FCSTD DOCUMENT  (FreeCAD 1.1R14555 (Git shallow))
Label: Instrument_Centipede
License: All rights reserved
LicenseURL: https://en.wikipedia.org/wiki/All_rights_reserved
objects: App::Link×95, App::Point×26, Assembly::AssemblyLink×25, App::FeaturePython×5, Assembly::JointGroup×1, Assembly::AssemblyObject×1
EXTERNAL_REF file=generated_example_K93-10436_all7_withTarantinorinos.FCStd obj=Assembly
EXTERNAL_REF file=generated_example_K93-10436_all7_withTarantinorinos.FCStd obj=K93_120
EXTERNAL_REF file=generated_example_K93-10436_all7_withTarantinorinos.FCStd obj=Reference_all7_1
EXTERNAL_REF file=generated_example_K93-10436_all7_withTarantinorinos.FCStd obj=Body
EXTERNAL_REF file=generated_example_K93-10436_all7_withTarantinorinos.FCStd obj=Assembly001
EXTERNAL_REF file=K93-10436-H7-L120_Tarantinorino_left_withFeet.FCStd obj=_3M_SJ5382
EXTERNAL_REF file=K93-10436-H7-L120_Tarantinorino_left_withFeet.FCStd obj=_3M_SJ5383
EXTERNAL_REF file=K93-10436-H7-L120_Tarantinorino_left_withFeet.FCStd obj=Body
EXTERNAL_REF file=generated_example_K93-10436_all7_withTarantinorinos.FCStd obj=Assembly002
EXTERNAL_REF file=generated_example_K93-10436_all7_withTarantinorinos.FCStd obj=Assembly003
EXTERNAL_REF file=K93-10436-H7-L120_Tarantinorino_right_withFeet.FCStd obj=Body__Mirror__1_
EXTERNAL_REF file=K93-10436-H7-L120_Tarantinorino_right_withFeet.FCStd obj=_3M_SJ5382
EXTERNAL_REF file=K93-10436-H7-L120_Tarantinorino_right_withFeet.FCStd obj=_3M_SJ5383
EXTERNAL_REF file=generated_example_K93-10436_all7_withTarantinorinos.FCStd obj=Assembly004
EXTERNAL_REF file=generated_example_K93-10436_all7_withTarantinorinos.FCStd obj=Body003
EXTERNAL_REF file=generated_example_K93-10436_all7_withTarantinorinos.FCStd obj=Body004
EXTERNAL_REF file=generated_example_K93-10436_all7_withTarantinorinos.FCStd obj=Body005
EXTERNAL_REF file=generated_example_K93-10436_all7_withTarantinorinos.FCStd obj=Body006

FEATURE [App::Point] Origin001
  Role = Origin
FEATURE [App::Point] Origin003
  Role = Origin
FEATURE [App::Link] K93_120  label="K93-120"
  LinkPlacement = pos=(0,126.938,111.562) rot=(1,0,0;1.5708rad)
  LinkedObject = -> <external generated_example_K93-10436_all7_withTarantinorinos.FCStd>#K93_120
  Placement = pos=(0,126.938,111.562) rot=(1,0,0;1.5708rad)
FEATURE [App::Link] Reference_all7_1  label="Reference_all7 1"
  LinkPlacement = pos=(2.87919,6.93809,110.59) rot=(0.99808,0,0;0rad)
  LinkedObject = -> <external generated_example_K93-10436_all7_withTarantinorinos.FCStd>#Reference_all7_1
  Placement = pos=(2.87919,6.93809,110.59) rot=(0.99808,0,0;0rad)
FEATURE [App::Link] Body
  LinkPlacement = pos=(2.87919,-53.8119,119.256) rot=(1,0,0;1.5708rad)
  LinkedObject = -> <external generated_example_K93-10436_all7_withTarantinorinos.FCStd>#Body
  Placement = pos=(2.87919,-53.8119,119.256) rot=(1,0,0;1.5708rad)
FEATURE [App::Point] Origin005  label="Origin006"
  Role = Origin
FEATURE [App::Link] _3M_SJ5382  label="3M_SJ5382"
  LinkPlacement = pos=(-30.6801,-1.9,-31) rot=(0.707107,0.707107,0;3.14159rad)
  LinkedObject = -> <external K93-10436-H7-L120_Tarantinorino_left_withFeet.FCStd>#_3M_SJ5382
  Placement = pos=(-30.6801,-1.9,-31) rot=(0.707107,0.707107,0;3.14159rad)
FEATURE [App::Link] _3M_SJ5383  label="3M_SJ5383"
  LinkPlacement = pos=(-9.29583,-1.9,-4.09999) rot=(0.57735,0.57735,0.57735;2.0944rad)
  LinkedObject = -> <external K93-10436-H7-L120_Tarantinorino_left_withFeet.FCStd>#_3M_SJ5383
  Placement = pos=(-9.29583,-1.9,-4.09999) rot=(0.57735,0.57735,0.57735;2.0944rad)
FEATURE [App::Link] Body001
  LinkPlacement = pos=(-62,-13.9,-4.09999) rot=(1,0,0;1.5708rad)
  LinkedObject = -> <external K93-10436-H7-L120_Tarantinorino_left_withFeet.FCStd>#Body
  Placement = pos=(-62,-13.9,-4.09999) rot=(1,0,0;1.5708rad)
FEATURE [Assembly::AssemblyLink] Assembly002  label="Assembly"
  Group = -> [_3M_SJ5382,_3M_SJ5383,Body001]
  LinkedObject = -> <external generated_example_K93-10436_all7_withTarantinorinos.FCStd>#Assembly001
  Origin = -> Origin004
  Placement = pos=(64.9193,-40.6619,123.46) rot=(0,0,1;0rad)
  Rigid = true
FEATURE [App::Point] Origin007  label="Origin009"
  Role = Origin
FEATURE [App::Link] _3M_SJ5384  label="3M_SJ5384"
  LinkPlacement = pos=(-30.6801,-1.9,-31) rot=(0.707107,0.707107,0;3.14159rad)
  LinkedObject = -> <external K93-10436-H7-L120_Tarantinorino_left_withFeet.FCStd>#_3M_SJ5382
  Placement = pos=(-30.6801,-1.9,-31) rot=(0.707107,0.707107,0;3.14159rad)
FEATURE [App::Link] _3M_SJ5385  label="3M_SJ5385"
  LinkPlacement = pos=(-9.29583,-1.9,-4.09999) rot=(0.57735,0.57735,0.57735;2.0944rad)
  LinkedObject = -> <external K93-10436-H7-L120_Tarantinorino_left_withFeet.FCStd>#_3M_SJ5383
  Placement = pos=(-9.29583,-1.9,-4.09999) rot=(0.57735,0.57735,0.57735;2.0944rad)
FEATURE [App::Link] Body002
  LinkPlacement = pos=(-62,-13.9,-4.09999) rot=(1,0,0;1.5708rad)
  LinkedObject = -> <external K93-10436-H7-L120_Tarantinorino_left_withFeet.FCStd>#Body
  Placement = pos=(-62,-13.9,-4.09999) rot=(1,0,0;1.5708rad)
FEATURE [Assembly::AssemblyLink] Assembly003  label="Assembly"
  Group = -> [_3M_SJ5384,_3M_SJ5385,Body002]
  LinkedObject = -> <external generated_example_K93-10436_all7_withTarantinorinos.FCStd>#Assembly002
  Origin = -> Origin006
  Placement = pos=(-59.1609,54.5381,123.46) rot=(0,0,1;3.14159rad)
  Rigid = true
FEATURE [App::Point] Origin009  label="Origin011"
  Role = Origin
FEATURE [App::Link] Body__Mirror__1_  label="Body (Mirror #1)"
  LinkPlacement = pos=(1.43051e-06,-13.9,-10.1) rot=(1,0,0;1.5708rad)
  LinkedObject = -> <external K93-10436-H7-L120_Tarantinorino_right_withFeet.FCStd>#Body__Mirror__1_
  Placement = pos=(1.43051e-06,-13.9,-10.1) rot=(1,0,0;1.5708rad)
FEATURE [App::Link] _3M_SJ5386  label="3M_SJ5386"
  LinkPlacement = pos=(-31.32,-1.89999,-37) rot=(0.707107,0.707107,0;3.14159rad)
  LinkedObject = -> <external K93-10436-H7-L120_Tarantinorino_right_withFeet.FCStd>#_3M_SJ5382
  Placement = pos=(-31.32,-1.89999,-37) rot=(0.707107,0.707107,0;3.14159rad)
FEATURE [App::Link] _3M_SJ5387  label="3M_SJ5387"
  LinkPlacement = pos=(-52.7042,-1.9,-10.1) rot=(-0.57735,-0.57735,0.57735;2.0944rad)
  LinkedObject = -> <external K93-10436-H7-L120_Tarantinorino_right_withFeet.FCStd>#_3M_SJ5383
  Placement = pos=(-52.7042,-1.9,-10.1) rot=(-0.57735,-0.57735,0.57735;2.0944rad)
FEATURE [Assembly::AssemblyLink] Assembly004  label="Assembly"
  Group = -> [Body__Mirror__1_,_3M_SJ5386,_3M_SJ5387]
  LinkedObject = -> <external generated_example_K93-10436_all7_withTarantinorinos.FCStd>#Assembly003
  Origin = -> Origin008
  Placement = pos=(2.91922,54.5381,129.46) rot=(0,0,1;3.14159rad)
  Rigid = true
FEATURE [App::Point] Origin011  label="Origin014"
  Role = Origin
FEATURE [App::Link] Body__Mirror__1_001  label="Body (Mirror #1)001"
  LinkPlacement = pos=(1.43051e-06,-13.9,-10.1) rot=(1,0,0;1.5708rad)
  LinkedObject = -> <external K93-10436-H7-L120_Tarantinorino_right_withFeet.FCStd>#Body__Mirror__1_
  Placement = pos=(1.43051e-06,-13.9,-10.1) rot=(1,0,0;1.5708rad)
FEATURE [App::Link] _3M_SJ5388  label="3M_SJ5388"
  LinkPlacement = pos=(-31.32,-1.89999,-37) rot=(0.707107,0.707107,0;3.14159rad)
  LinkedObject = -> <external K93-10436-H7-L120_Tarantinorino_right_withFeet.FCStd>#_3M_SJ5382
  Placement = pos=(-31.32,-1.89999,-37) rot=(0.707107,0.707107,0;3.14159rad)
FEATURE [App::Link] _3M_SJ5389  label="3M_SJ5389"
  LinkPlacement = pos=(-52.7042,-1.9,-10.1) rot=(-0.57735,-0.57735,0.57735;2.0944rad)
  LinkedObject = -> <external K93-10436-H7-L120_Tarantinorino_right_withFeet.FCStd>#_3M_SJ5383
  Placement = pos=(-52.7042,-1.9,-10.1) rot=(-0.57735,-0.57735,0.57735;2.0944rad)
FEATURE [Assembly::AssemblyLink] Assembly005  label="Assembly"
  Group = -> [Body__Mirror__1_001,_3M_SJ5388,_3M_SJ5389]
  LinkedObject = -> <external generated_example_K93-10436_all7_withTarantinorinos.FCStd>#Assembly004
  Origin = -> Origin010
  Placement = pos=(2.83915,-40.6619,129.251) rot=(0,0,1;0rad)
  Rigid = true
FEATURE [App::Link] Body003
  LinkPlacement = pos=(2.87919,-56.5619,119.047) rot=(1,0,0;1.5708rad)
  LinkedObject = -> <external generated_example_K93-10436_all7_withTarantinorinos.FCStd>#Body003
  Placement = pos=(2.87919,-56.5619,119.047) rot=(1,0,0;1.5708rad)
FEATURE [App::Link] Body004
  LinkPlacement = pos=(2.87919,-56.5619,119.256) rot=(0,0.707107,-0.707107;3.14159rad)
  LinkedObject = -> <external generated_example_K93-10436_all7_withTarantinorinos.FCStd>#Body004
  Placement = pos=(2.87919,-56.5619,119.256) rot=(0,0.707107,-0.707107;3.14159rad)
FEATURE [App::Link] Body005
  LinkPlacement = pos=(2.87919,70.4381,119.256) rot=(-1,0,0;1.5708rad)
  LinkedObject = -> <external generated_example_K93-10436_all7_withTarantinorinos.FCStd>#Body005
  Placement = pos=(2.87919,70.4381,119.256) rot=(-1,0,0;1.5708rad)
FEATURE [App::Link] Body006
  LinkPlacement = pos=(2.87919,70.4381,119.256) rot=(0,0.707107,0.707107;3.14159rad)
  LinkedObject = -> <external generated_example_K93-10436_all7_withTarantinorinos.FCStd>#Body006
  Placement = pos=(2.87919,70.4381,119.256) rot=(0,0.707107,0.707107;3.14159rad)
FEATURE [Assembly::AssemblyLink] Assembly001  label="Assembly"
  Group = -> [K93_120,Reference_all7_1,Body,Assembly002,Assembly003,Assembly004,Assembly005,Body003,Body004,Body005,Body006]
  LinkedObject = -> <external generated_example_K93-10436_all7_withTarantinorinos.FCStd>#Assembly
  Origin = -> Origin002
  Placement = pos=(-3.48643,-3.86422,0.740982) rot=(0,0,1;0rad)
  Rigid = true
FEATURE [App::Point] Origin013  label="Origin017"
  Role = Origin
FEATURE [App::Link] K93_121  label="K93-121"
  LinkPlacement = pos=(0,126.938,111.562) rot=(1,0,0;1.5708rad)
  LinkedObject = -> <external generated_example_K93-10436_all7_withTarantinorinos.FCStd>#K93_120
  Placement = pos=(0,126.938,111.562) rot=(1,0,0;1.5708rad)
FEATURE [App::Link] Reference_all7_001  label="Reference_all7 001"
  LinkPlacement = pos=(2.87919,6.93809,110.59) rot=(0.99808,0,0;0rad)
  LinkedObject = -> <external generated_example_K93-10436_all7_withTarantinorinos.FCStd>#Reference_all7_1
  Placement = pos=(2.87919,6.93809,110.59) rot=(0.99808,0,0;0rad)
FEATURE [App::Link] Body007
  LinkPlacement = pos=(2.87919,-53.8119,119.256) rot=(1,0,0;1.5708rad)
  LinkedObject = -> <external generated_example_K93-10436_all7_withTarantinorinos.FCStd>#Body
  Placement = pos=(2.87919,-53.8119,119.256) rot=(1,0,0;1.5708rad)
FEATURE [App::Point] Origin015  label="Origin020"
  Role = Origin
FEATURE [App::Link] _3M_SJ5390  label="3M_SJ5390"
  LinkPlacement = pos=(-30.6801,-1.9,-31) rot=(0.707107,0.707107,0;3.14159rad)
  LinkedObject = -> <external K93-10436-H7-L120_Tarantinorino_left_withFeet.FCStd>#_3M_SJ5382
  Placement = pos=(-30.6801,-1.9,-31) rot=(0.707107,0.707107,0;3.14159rad)
FEATURE [App::Link] _3M_SJ5391  label="3M_SJ5391"
  LinkPlacement = pos=(-9.29583,-1.9,-4.09999) rot=(0.57735,0.57735,0.57735;2.0944rad)
  LinkedObject = -> <external K93-10436-H7-L120_Tarantinorino_left_withFeet.FCStd>#_3M_SJ5383
  Placement = pos=(-9.29583,-1.9,-4.09999) rot=(0.57735,0.57735,0.57735;2.0944rad)
FEATURE [App::Link] Body008
  LinkPlacement = pos=(-62,-13.9,-4.09999) rot=(1,0,0;1.5708rad)
  LinkedObject = -> <external K93-10436-H7-L120_Tarantinorino_left_withFeet.FCStd>#Body
  Placement = pos=(-62,-13.9,-4.09999) rot=(1,0,0;1.5708rad)
FEATURE [Assembly::AssemblyLink] Assembly007  label="Assembly"
  Group = -> [_3M_SJ5390,_3M_SJ5391,Body008]
  LinkedObject = -> <external generated_example_K93-10436_all7_withTarantinorinos.FCStd>#Assembly001
  Origin = -> Origin014
  Placement = pos=(64.9193,-40.6619,123.46) rot=(0,0,1;0rad)
  Rigid = true
FEATURE [App::Point] Origin017  label="Origin022"
  Role = Origin
FEATURE [App::Link] _3M_SJ5392  label="3M_SJ5392"
  LinkPlacement = pos=(-30.6801,-1.9,-31) rot=(0.707107,0.707107,0;3.14159rad)
  LinkedObject = -> <external K93-10436-H7-L120_Tarantinorino_left_withFeet.FCStd>#_3M_SJ5382
  Placement = pos=(-30.6801,-1.9,-31) rot=(0.707107,0.707107,0;3.14159rad)
FEATURE [App::Link] _3M_SJ5393  label="3M_SJ5393"
  LinkPlacement = pos=(-9.29583,-1.9,-4.09999) rot=(0.57735,0.57735,0.57735;2.0944rad)
  LinkedObject = -> <external K93-10436-H7-L120_Tarantinorino_left_withFeet.FCStd>#_3M_SJ5383
  Placement = pos=(-9.29583,-1.9,-4.09999) rot=(0.57735,0.57735,0.57735;2.0944rad)
FEATURE [App::Link] Body009
  LinkPlacement = pos=(-62,-13.9,-4.09999) rot=(1,0,0;1.5708rad)
  LinkedObject = -> <external K93-10436-H7-L120_Tarantinorino_left_withFeet.FCStd>#Body
  Placement = pos=(-62,-13.9,-4.09999) rot=(1,0,0;1.5708rad)
FEATURE [Assembly::AssemblyLink] Assembly008  label="Assembly"
  Group = -> [_3M_SJ5392,_3M_SJ5393,Body009]
  LinkedObject = -> <external generated_example_K93-10436_all7_withTarantinorinos.FCStd>#Assembly002
  Origin = -> Origin016
  Placement = pos=(-59.1609,54.5381,123.46) rot=(0,0,1;3.14159rad)
  Rigid = true
FEATURE [App::Point] Origin019  label="Origin025"
  Role = Origin
FEATURE [App::Link] Body__Mirror__1_002  label="Body (Mirror #1)002"
  LinkPlacement = pos=(1.43051e-06,-13.9,-10.1) rot=(1,0,0;1.5708rad)
  LinkedObject = -> <external K93-10436-H7-L120_Tarantinorino_right_withFeet.FCStd>#Body__Mirror__1_
  Placement = pos=(1.43051e-06,-13.9,-10.1) rot=(1,0,0;1.5708rad)
FEATURE [App::Link] _3M_SJ5394  label="3M_SJ5394"
  LinkPlacement = pos=(-31.32,-1.89999,-37) rot=(0.707107,0.707107,0;3.14159rad)
  LinkedObject = -> <external K93-10436-H7-L120_Tarantinorino_right_withFeet.FCStd>#_3M_SJ5382
  Placement = pos=(-31.32,-1.89999,-37) rot=(0.707107,0.707107,0;3.14159rad)
FEATURE [App::Link] _3M_SJ5395  label="3M_SJ5395"
  LinkPlacement = pos=(-52.7042,-1.9,-10.1) rot=(-0.57735,-0.57735,0.57735;2.0944rad)
  LinkedObject = -> <external K93-10436-H7-L120_Tarantinorino_right_withFeet.FCStd>#_3M_SJ5383
  Placement = pos=(-52.7042,-1.9,-10.1) rot=(-0.57735,-0.57735,0.57735;2.0944rad)
FEATURE [Assembly::AssemblyLink] Assembly009  label="Assembly"
  Group = -> [Body__Mirror__1_002,_3M_SJ5394,_3M_SJ5395]
  LinkedObject = -> <external generated_example_K93-10436_all7_withTarantinorinos.FCStd>#Assembly003
  Origin = -> Origin018
  Placement = pos=(2.91922,54.5381,129.46) rot=(0,0,1;3.14159rad)
  Rigid = true
FEATURE [App::Point] Origin021  label="Origin028"
  Role = Origin
FEATURE [App::Link] Body__Mirror__1_003  label="Body (Mirror #1)003"
  LinkPlacement = pos=(1.43051e-06,-13.9,-10.1) rot=(1,0,0;1.5708rad)
  LinkedObject = -> <external K93-10436-H7-L120_Tarantinorino_right_withFeet.FCStd>#Body__Mirror__1_
  Placement = pos=(1.43051e-06,-13.9,-10.1) rot=(1,0,0;1.5708rad)
FEATURE [App::Link] _3M_SJ5396  label="3M_SJ5396"
  LinkPlacement = pos=(-31.32,-1.89999,-37) rot=(0.707107,0.707107,0;3.14159rad)
  LinkedObject = -> <external K93-10436-H7-L120_Tarantinorino_right_withFeet.FCStd>#_3M_SJ5382
  Placement = pos=(-31.32,-1.89999,-37) rot=(0.707107,0.707107,0;3.14159rad)
FEATURE [App::Link] _3M_SJ5397  label="3M_SJ5397"
  LinkPlacement = pos=(-52.7042,-1.9,-10.1) rot=(-0.57735,-0.57735,0.57735;2.0944rad)
  LinkedObject = -> <external K93-10436-H7-L120_Tarantinorino_right_withFeet.FCStd>#_3M_SJ5383
  Placement = pos=(-52.7042,-1.9,-10.1) rot=(-0.57735,-0.57735,0.57735;2.0944rad)
FEATURE [Assembly::AssemblyLink] Assembly010  label="Assembly"
  Group = -> [Body__Mirror__1_003,_3M_SJ5396,_3M_SJ5397]
  LinkedObject = -> <external generated_example_K93-10436_all7_withTarantinorinos.FCStd>#Assembly004
  Origin = -> Origin020
  Placement = pos=(2.83915,-40.6619,129.251) rot=(0,0,1;0rad)
  Rigid = true
FEATURE [App::Link] Body010
  LinkPlacement = pos=(2.87919,-56.5619,119.047) rot=(1,0,0;1.5708rad)
  LinkedObject = -> <external generated_example_K93-10436_all7_withTarantinorinos.FCStd>#Body003
  Placement = pos=(2.87919,-56.5619,119.047) rot=(1,0,0;1.5708rad)
FEATURE [App::Link] Body011
  LinkPlacement = pos=(2.87919,-56.5619,119.256) rot=(0,0.707107,-0.707107;3.14159rad)
  LinkedObject = -> <external generated_example_K93-10436_all7_withTarantinorinos.FCStd>#Body004
  Placement = pos=(2.87919,-56.5619,119.256) rot=(0,0.707107,-0.707107;3.14159rad)
FEATURE [App::Link] Body012
  LinkPlacement = pos=(2.87919,70.4381,119.256) rot=(-1,0,0;1.5708rad)
  LinkedObject = -> <external generated_example_K93-10436_all7_withTarantinorinos.FCStd>#Body005
  Placement = pos=(2.87919,70.4381,119.256) rot=(-1,0,0;1.5708rad)
FEATURE [App::Link] Body013
  LinkPlacement = pos=(2.87919,70.4381,119.256) rot=(0,0.707107,0.707107;3.14159rad)
  LinkedObject = -> <external generated_example_K93-10436_all7_withTarantinorinos.FCStd>#Body006
  Placement = pos=(2.87919,70.4381,119.256) rot=(0,0.707107,0.707107;3.14159rad)
FEATURE [Assembly::AssemblyLink] Assembly006  label="Assembly"
  Group = -> [K93_121,Reference_all7_001,Body007,Assembly007,Assembly008,Assembly009,Assembly010,Body010,Body011,Body012,Body013]
  LinkedObject = -> <external generated_example_K93-10436_all7_withTarantinorinos.FCStd>#Assembly
  Origin = -> Origin012
  Placement = pos=(-3.48643,-3.86423,48.941) rot=(0,0,1;0rad)
  Rigid = true
FEATURE [App::Point] Origin023  label="Origin031"
  Role = Origin
FEATURE [App::Link] K93_122  label="K93-122"
  LinkPlacement = pos=(0,126.938,111.562) rot=(1,0,0;1.5708rad)
  LinkedObject = -> <external generated_example_K93-10436_all7_withTarantinorinos.FCStd>#K93_120
  Placement = pos=(0,126.938,111.562) rot=(1,0,0;1.5708rad)
FEATURE [App::Link] Reference_all7_002  label="Reference_all7 002"
  LinkPlacement = pos=(2.87919,6.93809,110.59) rot=(0.99808,0,0;0rad)
  LinkedObject = -> <external generated_example_K93-10436_all7_withTarantinorinos.FCStd>#Reference_all7_1
  Placement = pos=(2.87919,6.93809,110.59) rot=(0.99808,0,0;0rad)
FEATURE [App::Link] Body014
  LinkPlacement = pos=(2.87919,-53.8119,119.256) rot=(1,0,0;1.5708rad)
  LinkedObject = -> <external generated_example_K93-10436_all7_withTarantinorinos.FCStd>#Body
  Placement = pos=(2.87919,-53.8119,119.256) rot=(1,0,0;1.5708rad)
FEATURE [App::Point] Origin025  label="Origin033"
  Role = Origin
FEATURE [App::Link] _3M_SJ5398  label="3M_SJ5398"
  LinkPlacement = pos=(-30.6801,-1.9,-31) rot=(0.707107,0.707107,0;3.14159rad)
  LinkedObject = -> <external K93-10436-H7-L120_Tarantinorino_left_withFeet.FCStd>#_3M_SJ5382
  Placement = pos=(-30.6801,-1.9,-31) rot=(0.707107,0.707107,0;3.14159rad)
FEATURE [App::Link] _3M_SJ5399  label="3M_SJ5399"
  LinkPlacement = pos=(-9.29583,-1.9,-4.09999) rot=(0.57735,0.57735,0.57735;2.0944rad)
  LinkedObject = -> <external K93-10436-H7-L120_Tarantinorino_left_withFeet.FCStd>#_3M_SJ5383
  Placement = pos=(-9.29583,-1.9,-4.09999) rot=(0.57735,0.57735,0.57735;2.0944rad)
FEATURE [App::Link] Body015
  LinkPlacement = pos=(-62,-13.9,-4.09999) rot=(1,0,0;1.5708rad)
  LinkedObject = -> <external K93-10436-H7-L120_Tarantinorino_left_withFeet.FCStd>#Body
  Placement = pos=(-62,-13.9,-4.09999) rot=(1,0,0;1.5708rad)
FEATURE [Assembly::AssemblyLink] Assembly012  label="Assembly"
  Group = -> [_3M_SJ5398,_3M_SJ5399,Body015]
  LinkedObject = -> <external generated_example_K93-10436_all7_withTarantinorinos.FCStd>#Assembly001
  Origin = -> Origin024
  Placement = pos=(64.9193,-40.6619,123.46) rot=(0,0,1;0rad)
  Rigid = true
FEATURE [App::Point] Origin027  label="Origin036"
  Role = Origin
FEATURE [App::Link] _3M_SJ5400  label="3M_SJ5400"
  LinkPlacement = pos=(-30.6801,-1.9,-31) rot=(0.707107,0.707107,0;3.14159rad)
  LinkedObject = -> <external K93-10436-H7-L120_Tarantinorino_left_withFeet.FCStd>#_3M_SJ5382
  Placement = pos=(-30.6801,-1.9,-31) rot=(0.707107,0.707107,0;3.14159rad)
FEATURE [App::Link] _3M_SJ5401  label="3M_SJ5401"
  LinkPlacement = pos=(-9.29583,-1.9,-4.09999) rot=(0.57735,0.57735,0.57735;2.0944rad)
  LinkedObject = -> <external K93-10436-H7-L120_Tarantinorino_left_withFeet.FCStd>#_3M_SJ5383
  Placement = pos=(-9.29583,-1.9,-4.09999) rot=(0.57735,0.57735,0.57735;2.0944rad)
FEATURE [App::Link] Body016
  LinkPlacement = pos=(-62,-13.9,-4.09999) rot=(1,0,0;1.5708rad)
  LinkedObject = -> <external K93-10436-H7-L120_Tarantinorino_left_withFeet.FCStd>#Body
  Placement = pos=(-62,-13.9,-4.09999) rot=(1,0,0;1.5708rad)
FEATURE [Assembly::AssemblyLink] Assembly013  label="Assembly"
  Group = -> [_3M_SJ5400,_3M_SJ5401,Body016]
  LinkedObject = -> <external generated_example_K93-10436_all7_withTarantinorinos.FCStd>#Assembly002
  Origin = -> Origin026
  Placement = pos=(-59.1609,54.5381,123.46) rot=(0,0,1;3.14159rad)
  Rigid = true
FEATURE [App::Point] Origin029  label="Origin039"
  Role = Origin
FEATURE [App::Link] Body__Mirror__1_004  label="Body (Mirror #1)004"
  LinkPlacement = pos=(1.43051e-06,-13.9,-10.1) rot=(1,0,0;1.5708rad)
  LinkedObject = -> <external K93-10436-H7-L120_Tarantinorino_right_withFeet.FCStd>#Body__Mirror__1_
  Placement = pos=(1.43051e-06,-13.9,-10.1) rot=(1,0,0;1.5708rad)
FEATURE [App::Link] _3M_SJ5402  label="3M_SJ5402"
  LinkPlacement = pos=(-31.32,-1.89999,-37) rot=(0.707107,0.707107,0;3.14159rad)
  LinkedObject = -> <external K93-10436-H7-L120_Tarantinorino_right_withFeet.FCStd>#_3M_SJ5382
  Placement = pos=(-31.32,-1.89999,-37) rot=(0.707107,0.707107,0;3.14159rad)
FEATURE [App::Link] _3M_SJ5403  label="3M_SJ5403"
  LinkPlacement = pos=(-52.7042,-1.9,-10.1) rot=(-0.57735,-0.57735,0.57735;2.0944rad)
  LinkedObject = -> <external K93-10436-H7-L120_Tarantinorino_right_withFeet.FCStd>#_3M_SJ5383
  Placement = pos=(-52.7042,-1.9,-10.1) rot=(-0.57735,-0.57735,0.57735;2.0944rad)
FEATURE [Assembly::AssemblyLink] Assembly014  label="Assembly"
  Group = -> [Body__Mirror__1_004,_3M_SJ5402,_3M_SJ5403]
  LinkedObject = -> <external generated_example_K93-10436_all7_withTarantinorinos.FCStd>#Assembly003
  Origin = -> Origin028
  Placement = pos=(2.91922,54.5381,129.46) rot=(0,0,1;3.14159rad)
  Rigid = true
FEATURE [App::Point] Origin031  label="Origin041"
  Role = Origin
FEATURE [App::Link] Body__Mirror__1_005  label="Body (Mirror #1)005"
  LinkPlacement = pos=(1.43051e-06,-13.9,-10.1) rot=(1,0,0;1.5708rad)
  LinkedObject = -> <external K93-10436-H7-L120_Tarantinorino_right_withFeet.FCStd>#Body__Mirror__1_
  Placement = pos=(1.43051e-06,-13.9,-10.1) rot=(1,0,0;1.5708rad)
FEATURE [App::Link] _3M_SJ5404  label="3M_SJ5404"
  LinkPlacement = pos=(-31.32,-1.89999,-37) rot=(0.707107,0.707107,0;3.14159rad)
  LinkedObject = -> <external K93-10436-H7-L120_Tarantinorino_right_withFeet.FCStd>#_3M_SJ5382
  Placement = pos=(-31.32,-1.89999,-37) rot=(0.707107,0.707107,0;3.14159rad)
FEATURE [App::Link] _3M_SJ5405  label="3M_SJ5405"
  LinkPlacement = pos=(-52.7042,-1.9,-10.1) rot=(-0.57735,-0.57735,0.57735;2.0944rad)
  LinkedObject = -> <external K93-10436-H7-L120_Tarantinorino_right_withFeet.FCStd>#_3M_SJ5383
  Placement = pos=(-52.7042,-1.9,-10.1) rot=(-0.57735,-0.57735,0.57735;2.0944rad)
FEATURE [Assembly::AssemblyLink] Assembly015  label="Assembly"
  Group = -> [Body__Mirror__1_005,_3M_SJ5404,_3M_SJ5405]
  LinkedObject = -> <external generated_example_K93-10436_all7_withTarantinorinos.FCStd>#Assembly004
  Origin = -> Origin030
  Placement = pos=(2.83915,-40.6619,129.251) rot=(0,0,1;0rad)
  Rigid = true
FEATURE [App::Link] Body017
  LinkPlacement = pos=(2.87919,-56.5619,119.047) rot=(1,0,0;1.5708rad)
  LinkedObject = -> <external generated_example_K93-10436_all7_withTarantinorinos.FCStd>#Body003
  Placement = pos=(2.87919,-56.5619,119.047) rot=(1,0,0;1.5708rad)
FEATURE [App::Link] Body018
  LinkPlacement = pos=(2.87919,-56.5619,119.256) rot=(0,0.707107,-0.707107;3.14159rad)
  LinkedObject = -> <external generated_example_K93-10436_all7_withTarantinorinos.FCStd>#Body004
  Placement = pos=(2.87919,-56.5619,119.256) rot=(0,0.707107,-0.707107;3.14159rad)
FEATURE [App::Link] Body019
  LinkPlacement = pos=(2.87919,70.4381,119.256) rot=(-1,0,0;1.5708rad)
  LinkedObject = -> <external generated_example_K93-10436_all7_withTarantinorinos.FCStd>#Body005
  Placement = pos=(2.87919,70.4381,119.256) rot=(-1,0,0;1.5708rad)
FEATURE [App::Link] Body020
  LinkPlacement = pos=(2.87919,70.4381,119.256) rot=(0,0.707107,0.707107;3.14159rad)
  LinkedObject = -> <external generated_example_K93-10436_all7_withTarantinorinos.FCStd>#Body006
  Placement = pos=(2.87919,70.4381,119.256) rot=(0,0.707107,0.707107;3.14159rad)
FEATURE [Assembly::AssemblyLink] Assembly011  label="Assembly"
  Group = -> [K93_122,Reference_all7_002,Body014,Assembly012,Assembly013,Assembly014,Assembly015,Body017,Body018,Body019,Body020]
  LinkedObject = -> <external generated_example_K93-10436_all7_withTarantinorinos.FCStd>#Assembly
  Origin = -> Origin022
  Placement = pos=(-3.48643,-3.86424,97.141) rot=(0,0,1;0rad)
  Rigid = true
FEATURE [App::Point] Origin033  label="Origin044"
  Role = Origin
FEATURE [App::Link] K93_123  label="K93-123"
  LinkPlacement = pos=(0,126.938,111.562) rot=(1,0,0;1.5708rad)
  LinkedObject = -> <external generated_example_K93-10436_all7_withTarantinorinos.FCStd>#K93_120
  Placement = pos=(0,126.938,111.562) rot=(1,0,0;1.5708rad)
FEATURE [App::Link] Reference_all7_003  label="Reference_all7 003"
  LinkPlacement = pos=(2.87919,6.93809,110.59) rot=(0.99808,0,0;0rad)
  LinkedObject = -> <external generated_example_K93-10436_all7_withTarantinorinos.FCStd>#Reference_all7_1
  Placement = pos=(2.87919,6.93809,110.59) rot=(0.99808,0,0;0rad)
FEATURE [App::Link] Body021
  LinkPlacement = pos=(2.87919,-53.8119,119.256) rot=(1,0,0;1.5708rad)
  LinkedObject = -> <external generated_example_K93-10436_all7_withTarantinorinos.FCStd>#Body
  Placement = pos=(2.87919,-53.8119,119.256) rot=(1,0,0;1.5708rad)
FEATURE [App::Point] Origin035  label="Origin047"
  Role = Origin
FEATURE [App::Link] _3M_SJ5406  label="3M_SJ5406"
  LinkPlacement = pos=(-30.6801,-1.9,-31) rot=(0.707107,0.707107,0;3.14159rad)
  LinkedObject = -> <external K93-10436-H7-L120_Tarantinorino_left_withFeet.FCStd>#_3M_SJ5382
  Placement = pos=(-30.6801,-1.9,-31) rot=(0.707107,0.707107,0;3.14159rad)
FEATURE [App::Link] _3M_SJ5407  label="3M_SJ5407"
  LinkPlacement = pos=(-9.29583,-1.9,-4.09999) rot=(0.57735,0.57735,0.57735;2.0944rad)
  LinkedObject = -> <external K93-10436-H7-L120_Tarantinorino_left_withFeet.FCStd>#_3M_SJ5383
  Placement = pos=(-9.29583,-1.9,-4.09999) rot=(0.57735,0.57735,0.57735;2.0944rad)
FEATURE [App::Link] Body022
  LinkPlacement = pos=(-62,-13.9,-4.09999) rot=(1,0,0;1.5708rad)
  LinkedObject = -> <external K93-10436-H7-L120_Tarantinorino_left_withFeet.FCStd>#Body
  Placement = pos=(-62,-13.9,-4.09999) rot=(1,0,0;1.5708rad)
FEATURE [Assembly::AssemblyLink] Assembly017  label="Assembly"
  Group = -> [_3M_SJ5406,_3M_SJ5407,Body022]
  LinkedObject = -> <external generated_example_K93-10436_all7_withTarantinorinos.FCStd>#Assembly001
  Origin = -> Origin034
  Placement = pos=(64.9193,-40.6619,123.46) rot=(0,0,1;0rad)
  Rigid = true
FEATURE [App::Point] Origin037  label="Origin050"
  Role = Origin
FEATURE [App::Link] _3M_SJ5408  label="3M_SJ5408"
  LinkPlacement = pos=(-30.6801,-1.9,-31) rot=(0.707107,0.707107,0;3.14159rad)
  LinkedObject = -> <external K93-10436-H7-L120_Tarantinorino_left_withFeet.FCStd>#_3M_SJ5382
  Placement = pos=(-30.6801,-1.9,-31) rot=(0.707107,0.707107,0;3.14159rad)
FEATURE [App::Link] _3M_SJ5409  label="3M_SJ5409"
  LinkPlacement = pos=(-9.29583,-1.9,-4.09999) rot=(0.57735,0.57735,0.57735;2.0944rad)
  LinkedObject = -> <external K93-10436-H7-L120_Tarantinorino_left_withFeet.FCStd>#_3M_SJ5383
  Placement = pos=(-9.29583,-1.9,-4.09999) rot=(0.57735,0.57735,0.57735;2.0944rad)
FEATURE [App::Link] Body023
  LinkPlacement = pos=(-62,-13.9,-4.09999) rot=(1,0,0;1.5708rad)
  LinkedObject = -> <external K93-10436-H7-L120_Tarantinorino_left_withFeet.FCStd>#Body
  Placement = pos=(-62,-13.9,-4.09999) rot=(1,0,0;1.5708rad)
FEATURE [Assembly::AssemblyLink] Assembly018  label="Assembly"
  Group = -> [_3M_SJ5408,_3M_SJ5409,Body023]
  LinkedObject = -> <external generated_example_K93-10436_all7_withTarantinorinos.FCStd>#Assembly002
  Origin = -> Origin036
  Placement = pos=(-59.1609,54.5381,123.46) rot=(0,0,1;3.14159rad)
  Rigid = true
FEATURE [App::Point] Origin039  label="Origin052"
  Role = Origin
FEATURE [App::Link] Body__Mirror__1_006  label="Body (Mirror #1)006"
  LinkPlacement = pos=(1.43051e-06,-13.9,-10.1) rot=(1,0,0;1.5708rad)
  LinkedObject = -> <external K93-10436-H7-L120_Tarantinorino_right_withFeet.FCStd>#Body__Mirror__1_
  Placement = pos=(1.43051e-06,-13.9,-10.1) rot=(1,0,0;1.5708rad)
FEATURE [App::Link] _3M_SJ5410  label="3M_SJ5410"
  LinkPlacement = pos=(-31.32,-1.89999,-37) rot=(0.707107,0.707107,0;3.14159rad)
  LinkedObject = -> <external K93-10436-H7-L120_Tarantinorino_right_withFeet.FCStd>#_3M_SJ5382
  Placement = pos=(-31.32,-1.89999,-37) rot=(0.707107,0.707107,0;3.14159rad)
FEATURE [App::Link] _3M_SJ5411  label="3M_SJ5411"
  LinkPlacement = pos=(-52.7042,-1.9,-10.1) rot=(-0.57735,-0.57735,0.57735;2.0944rad)
  LinkedObject = -> <external K93-10436-H7-L120_Tarantinorino_right_withFeet.FCStd>#_3M_SJ5383
  Placement = pos=(-52.7042,-1.9,-10.1) rot=(-0.57735,-0.57735,0.57735;2.0944rad)
FEATURE [Assembly::AssemblyLink] Assembly019  label="Assembly"
  Group = -> [Body__Mirror__1_006,_3M_SJ5410,_3M_SJ5411]
  LinkedObject = -> <external generated_example_K93-10436_all7_withTarantinorinos.FCStd>#Assembly003
  Origin = -> Origin038
  Placement = pos=(2.91922,54.5381,129.46) rot=(0,0,1;3.14159rad)
  Rigid = true
FEATURE [App::Point] Origin041  label="Origin055"
  Role = Origin
FEATURE [App::Link] Body__Mirror__1_007  label="Body (Mirror #1)007"
  LinkPlacement = pos=(1.43051e-06,-13.9,-10.1) rot=(1,0,0;1.5708rad)
  LinkedObject = -> <external K93-10436-H7-L120_Tarantinorino_right_withFeet.FCStd>#Body__Mirror__1_
  Placement = pos=(1.43051e-06,-13.9,-10.1) rot=(1,0,0;1.5708rad)
FEATURE [App::Link] _3M_SJ5412  label="3M_SJ5412"
  LinkPlacement = pos=(-31.32,-1.89999,-37) rot=(0.707107,0.707107,0;3.14159rad)
  LinkedObject = -> <external K93-10436-H7-L120_Tarantinorino_right_withFeet.FCStd>#_3M_SJ5382
  Placement = pos=(-31.32,-1.89999,-37) rot=(0.707107,0.707107,0;3.14159rad)
FEATURE [App::Link] _3M_SJ5413  label="3M_SJ5413"
  LinkPlacement = pos=(-52.7042,-1.9,-10.1) rot=(-0.57735,-0.57735,0.57735;2.0944rad)
  LinkedObject = -> <external K93-10436-H7-L120_Tarantinorino_right_withFeet.FCStd>#_3M_SJ5383
  Placement = pos=(-52.7042,-1.9,-10.1) rot=(-0.57735,-0.57735,0.57735;2.0944rad)
FEATURE [Assembly::AssemblyLink] Assembly020  label="Assembly"
  Group = -> [Body__Mirror__1_007,_3M_SJ5412,_3M_SJ5413]
  LinkedObject = -> <external generated_example_K93-10436_all7_withTarantinorinos.FCStd>#Assembly004
  Origin = -> Origin040
  Placement = pos=(2.83915,-40.6619,129.251) rot=(0,0,1;0rad)
  Rigid = true
FEATURE [App::Link] Body024
  LinkPlacement = pos=(2.87919,-56.5619,119.047) rot=(1,0,0;1.5708rad)
  LinkedObject = -> <external generated_example_K93-10436_all7_withTarantinorinos.FCStd>#Body003
  Placement = pos=(2.87919,-56.5619,119.047) rot=(1,0,0;1.5708rad)
FEATURE [App::Link] Body025
  LinkPlacement = pos=(2.87919,-56.5619,119.256) rot=(0,0.707107,-0.707107;3.14159rad)
  LinkedObject = -> <external generated_example_K93-10436_all7_withTarantinorinos.FCStd>#Body004
  Placement = pos=(2.87919,-56.5619,119.256) rot=(0,0.707107,-0.707107;3.14159rad)
FEATURE [App::Link] Body026
  LinkPlacement = pos=(2.87919,70.4381,119.256) rot=(-1,0,0;1.5708rad)
  LinkedObject = -> <external generated_example_K93-10436_all7_withTarantinorinos.FCStd>#Body005
  Placement = pos=(2.87919,70.4381,119.256) rot=(-1,0,0;1.5708rad)
FEATURE [App::Link] Body027
  LinkPlacement = pos=(2.87919,70.4381,119.256) rot=(0,0.707107,0.707107;3.14159rad)
  LinkedObject = -> <external generated_example_K93-10436_all7_withTarantinorinos.FCStd>#Body006
  Placement = pos=(2.87919,70.4381,119.256) rot=(0,0.707107,0.707107;3.14159rad)
FEATURE [Assembly::AssemblyLink] Assembly016  label="Assembly"
  Group = -> [K93_123,Reference_all7_003,Body021,Assembly017,Assembly018,Assembly019,Assembly020,Body024,Body025,Body026,Body027]
  LinkedObject = -> <external generated_example_K93-10436_all7_withTarantinorinos.FCStd>#Assembly
  Origin = -> Origin032
  Placement = pos=(-3.48643,-3.86424,145.341) rot=(0,0,1;0rad)
  Rigid = true
FEATURE [App::Point] Origin043  label="Origin058"
  Role = Origin
FEATURE [App::Link] K93_124  label="K93-124"
  LinkPlacement = pos=(0,126.938,111.562) rot=(1,0,0;1.5708rad)
  LinkedObject = -> <external generated_example_K93-10436_all7_withTarantinorinos.FCStd>#K93_120
  Placement = pos=(0,126.938,111.562) rot=(1,0,0;1.5708rad)
FEATURE [App::Link] Reference_all7_004  label="Reference_all7 004"
  LinkPlacement = pos=(2.87919,6.93809,110.59) rot=(0.99808,0,0;0rad)
  LinkedObject = -> <external generated_example_K93-10436_all7_withTarantinorinos.FCStd>#Reference_all7_1
  Placement = pos=(2.87919,6.93809,110.59) rot=(0.99808,0,0;0rad)
FEATURE [App::Link] Body028
  LinkPlacement = pos=(2.87919,-53.8119,119.256) rot=(1,0,0;1.5708rad)
  LinkedObject = -> <external generated_example_K93-10436_all7_withTarantinorinos.FCStd>#Body
  Placement = pos=(2.87919,-53.8119,119.256) rot=(1,0,0;1.5708rad)
FEATURE [App::Point] Origin045  label="Origin061"
  Role = Origin
FEATURE [App::Link] _3M_SJ5414  label="3M_SJ5414"
  LinkPlacement = pos=(-30.6801,-1.9,-31) rot=(0.707107,0.707107,0;3.14159rad)
  LinkedObject = -> <external K93-10436-H7-L120_Tarantinorino_left_withFeet.FCStd>#_3M_SJ5382
  Placement = pos=(-30.6801,-1.9,-31) rot=(0.707107,0.707107,0;3.14159rad)
FEATURE [App::Link] _3M_SJ5415  label="3M_SJ5415"
  LinkPlacement = pos=(-9.29583,-1.9,-4.09999) rot=(0.57735,0.57735,0.57735;2.0944rad)
  LinkedObject = -> <external K93-10436-H7-L120_Tarantinorino_left_withFeet.FCStd>#_3M_SJ5383
  Placement = pos=(-9.29583,-1.9,-4.09999) rot=(0.57735,0.57735,0.57735;2.0944rad)
FEATURE [App::Link] Body029
  LinkPlacement = pos=(-62,-13.9,-4.09999) rot=(1,0,0;1.5708rad)
  LinkedObject = -> <external K93-10436-H7-L120_Tarantinorino_left_withFeet.FCStd>#Body
  Placement = pos=(-62,-13.9,-4.09999) rot=(1,0,0;1.5708rad)
FEATURE [Assembly::AssemblyLink] Assembly022  label="Assembly"
  Group = -> [_3M_SJ5414,_3M_SJ5415,Body029]
  LinkedObject = -> <external generated_example_K93-10436_all7_withTarantinorinos.FCStd>#Assembly001
  Origin = -> Origin044
  Placement = pos=(64.9193,-40.6619,123.46) rot=(0,0,1;0rad)
  Rigid = true
FEATURE [App::Point] Origin047  label="Origin063"
  Role = Origin
FEATURE [App::Link] _3M_SJ5416  label="3M_SJ5416"
  LinkPlacement = pos=(-30.6801,-1.9,-31) rot=(0.707107,0.707107,0;3.14159rad)
  LinkedObject = -> <external K93-10436-H7-L120_Tarantinorino_left_withFeet.FCStd>#_3M_SJ5382
  Placement = pos=(-30.6801,-1.9,-31) rot=(0.707107,0.707107,0;3.14159rad)
FEATURE [App::Link] _3M_SJ5417  label="3M_SJ5417"
  LinkPlacement = pos=(-9.29583,-1.9,-4.09999) rot=(0.57735,0.57735,0.57735;2.0944rad)
  LinkedObject = -> <external K93-10436-H7-L120_Tarantinorino_left_withFeet.FCStd>#_3M_SJ5383
  Placement = pos=(-9.29583,-1.9,-4.09999) rot=(0.57735,0.57735,0.57735;2.0944rad)
FEATURE [App::Link] Body030
  LinkPlacement = pos=(-62,-13.9,-4.09999) rot=(1,0,0;1.5708rad)
  LinkedObject = -> <external K93-10436-H7-L120_Tarantinorino_left_withFeet.FCStd>#Body
  Placement = pos=(-62,-13.9,-4.09999) rot=(1,0,0;1.5708rad)
FEATURE [Assembly::AssemblyLink] Assembly023  label="Assembly"
  Group = -> [_3M_SJ5416,_3M_SJ5417,Body030]
  LinkedObject = -> <external generated_example_K93-10436_all7_withTarantinorinos.FCStd>#Assembly002
  Origin = -> Origin046
  Placement = pos=(-59.1609,54.5381,123.46) rot=(0,0,1;3.14159rad)
  Rigid = true
FEATURE [App::Point] Origin049  label="Origin066"
  Role = Origin
FEATURE [App::Link] Body__Mirror__1_008  label="Body (Mirror #1)008"
  LinkPlacement = pos=(1.43051e-06,-13.9,-10.1) rot=(1,0,0;1.5708rad)
  LinkedObject = -> <external K93-10436-H7-L120_Tarantinorino_right_withFeet.FCStd>#Body__Mirror__1_
  Placement = pos=(1.43051e-06,-13.9,-10.1) rot=(1,0,0;1.5708rad)
FEATURE [App::Link] _3M_SJ5418  label="3M_SJ5418"
  LinkPlacement = pos=(-31.32,-1.89999,-37) rot=(0.707107,0.707107,0;3.14159rad)
  LinkedObject = -> <external K93-10436-H7-L120_Tarantinorino_right_withFeet.FCStd>#_3M_SJ5382
  Placement = pos=(-31.32,-1.89999,-37) rot=(0.707107,0.707107,0;3.14159rad)
FEATURE [App::Link] _3M_SJ5419  label="3M_SJ5419"
  LinkPlacement = pos=(-52.7042,-1.9,-10.1) rot=(-0.57735,-0.57735,0.57735;2.0944rad)
  LinkedObject = -> <external K93-10436-H7-L120_Tarantinorino_right_withFeet.FCStd>#_3M_SJ5383
  Placement = pos=(-52.7042,-1.9,-10.1) rot=(-0.57735,-0.57735,0.57735;2.0944rad)
FEATURE [Assembly::AssemblyLink] Assembly024  label="Assembly"
  Group = -> [Body__Mirror__1_008,_3M_SJ5418,_3M_SJ5419]
  LinkedObject = -> <external generated_example_K93-10436_all7_withTarantinorinos.FCStd>#Assembly003
  Origin = -> Origin048
  Placement = pos=(2.91922,54.5381,129.46) rot=(0,0,1;3.14159rad)
  Rigid = true
FEATURE [App::Point] Origin051  label="Origin069"
  Role = Origin
FEATURE [App::Link] Body__Mirror__1_009  label="Body (Mirror #1)009"
  LinkPlacement = pos=(1.43051e-06,-13.9,-10.1) rot=(1,0,0;1.5708rad)
  LinkedObject = -> <external K93-10436-H7-L120_Tarantinorino_right_withFeet.FCStd>#Body__Mirror__1_
  Placement = pos=(1.43051e-06,-13.9,-10.1) rot=(1,0,0;1.5708rad)
FEATURE [App::Link] _3M_SJ5420  label="3M_SJ5420"
  LinkPlacement = pos=(-31.32,-1.89999,-37) rot=(0.707107,0.707107,0;3.14159rad)
  LinkedObject = -> <external K93-10436-H7-L120_Tarantinorino_right_withFeet.FCStd>#_3M_SJ5382
  Placement = pos=(-31.32,-1.89999,-37) rot=(0.707107,0.707107,0;3.14159rad)
FEATURE [App::Link] _3M_SJ5421  label="3M_SJ5421"
  LinkPlacement = pos=(-52.7042,-1.9,-10.1) rot=(-0.57735,-0.57735,0.57735;2.0944rad)
  LinkedObject = -> <external K93-10436-H7-L120_Tarantinorino_right_withFeet.FCStd>#_3M_SJ5383
  Placement = pos=(-52.7042,-1.9,-10.1) rot=(-0.57735,-0.57735,0.57735;2.0944rad)
FEATURE [Assembly::AssemblyLink] Assembly025  label="Assembly"
  Group = -> [Body__Mirror__1_009,_3M_SJ5420,_3M_SJ5421]
  LinkedObject = -> <external generated_example_K93-10436_all7_withTarantinorinos.FCStd>#Assembly004
  Origin = -> Origin050
  Placement = pos=(2.83915,-40.6619,129.251) rot=(0,0,1;0rad)
  Rigid = true
FEATURE [App::Link] Body031
  LinkPlacement = pos=(2.87919,-56.5619,119.047) rot=(1,0,0;1.5708rad)
  LinkedObject = -> <external generated_example_K93-10436_all7_withTarantinorinos.FCStd>#Body003
  Placement = pos=(2.87919,-56.5619,119.047) rot=(1,0,0;1.5708rad)
FEATURE [App::Link] Body032
  LinkPlacement = pos=(2.87919,-56.5619,119.256) rot=(0,0.707107,-0.707107;3.14159rad)
  LinkedObject = -> <external generated_example_K93-10436_all7_withTarantinorinos.FCStd>#Body004
  Placement = pos=(2.87919,-56.5619,119.256) rot=(0,0.707107,-0.707107;3.14159rad)
FEATURE [App::Link] Body033
  LinkPlacement = pos=(2.87919,70.4381,119.256) rot=(-1,0,0;1.5708rad)
  LinkedObject = -> <external generated_example_K93-10436_all7_withTarantinorinos.FCStd>#Body005
  Placement = pos=(2.87919,70.4381,119.256) rot=(-1,0,0;1.5708rad)
FEATURE [App::Link] Body034
  LinkPlacement = pos=(2.87919,70.4381,119.256) rot=(0,0.707107,0.707107;3.14159rad)
  LinkedObject = -> <external generated_example_K93-10436_all7_withTarantinorinos.FCStd>#Body006
  Placement = pos=(2.87919,70.4381,119.256) rot=(0,0.707107,0.707107;3.14159rad)
FEATURE [Assembly::AssemblyLink] Assembly021  label="Assembly"
  Group = -> [K93_124,Reference_all7_004,Body028,Assembly022,Assembly023,Assembly024,Assembly025,Body031,Body032,Body033,Body034]
  LinkedObject = -> <external generated_example_K93-10436_all7_withTarantinorinos.FCStd>#Assembly
  Origin = -> Origin042
  Placement = pos=(-3.48643,-3.86425,193.541) rot=(0,0,1;0rad)
  Rigid = true
FEATURE [App::FeaturePython] Joint  label="Fixed"  # Assembly joint (typed FeaturePython)
  Angle = 0
  AngleMax = 0
  AngleMin = 0
  Detach1 = false
  Detach2 = false
  Distance = 0
  Distance2 = 0
  EnableAngleMax = false
  EnableAngleMin = false
  EnableLengthMax = false
  EnableLengthMin = false
  JointType = 0 (Fixed)
  LengthMax = 0
  LengthMin = 0
  Placement1 = pos=(31.32,-24.1,1) rot=(0.707107,0,0.707107;3.14159rad)
  Placement2 = pos=(31.32,24.1,1) rot=(0.707107,0,0.707107;3.14159rad)
  Reference1 = -> Assembly [Assembly006.Assembly007.Body008.Edge120,Assembly006.Assembly007.Body008.Edge120]
  Reference2 = -> Assembly [Assembly001.Assembly002.Body001.Edge112,Assembly001.Assembly002.Body001.Edge112]
  Suppressed = false
FEATURE [App::FeaturePython] GroundedJoint  # Assembly grounded joint (typed FeaturePython)
  ObjectToGround = -> Assembly001
FEATURE [App::FeaturePython] Joint001  label="Fixed001"  # Assembly joint (typed FeaturePython)
  Angle = 0
  AngleMax = 0
  AngleMin = 0
  Detach1 = false
  Detach2 = false
  Distance = 0
  Distance2 = 0
  EnableAngleMax = false
  EnableAngleMin = false
  EnableLengthMax = false
  EnableLengthMin = false
  JointType = 0 (Fixed)
  LengthMax = 0
  LengthMin = 0
  Placement1 = pos=(31.32,-24.1,1) rot=(0.707107,0,0.707107;3.14159rad)
  Placement2 = pos=(31.32,24.1,1) rot=(0.707107,0,0.707107;3.14159rad)
  Reference1 = -> Assembly [Assembly011.Assembly012.Body015.Edge120,Assembly011.Assembly012.Body015.Edge120]
  Reference2 = -> Assembly [Assembly006.Assembly007.Body008.Edge112,Assembly006.Assembly007.Body008.Edge112]
  Suppressed = false
FEATURE [App::FeaturePython] Joint002  label="Fixed002"  # Assembly joint (typed FeaturePython)
  Angle = 0
  AngleMax = 0
  AngleMin = 0
  Detach1 = false
  Detach2 = false
  Distance = 0
  Distance2 = 0
  EnableAngleMax = false
  EnableAngleMin = false
  EnableLengthMax = false
  EnableLengthMin = false
  JointType = 0 (Fixed)
  LengthMax = 0
  LengthMin = 0
  Placement1 = pos=(31.32,24.1,1) rot=(0.707107,0,0.707107;3.14159rad)
  Placement2 = pos=(31.32,-24.1,1) rot=(0.707107,0,0.707107;3.14159rad)
  Reference1 = -> Assembly [Assembly011.Assembly012.Body015.Edge112,Assembly011.Assembly012.Body015.Edge112]
  Reference2 = -> Assembly [Assembly016.Assembly017.Body022.Edge120,Assembly016.Assembly017.Body022.Edge120]
  Suppressed = false
FEATURE [App::FeaturePython] Joint003  label="Fixed003"  # Assembly joint (typed FeaturePython)
  Angle = 0
  AngleMax = 0
  AngleMin = 0
  Detach1 = false
  Detach2 = false
  Distance = 0
  Distance2 = 0
  EnableAngleMax = false
  EnableAngleMin = false
  EnableLengthMax = false
  EnableLengthMin = false
  JointType = 0 (Fixed)
  LengthMax = 0
  LengthMin = 0
  Placement1 = pos=(31.32,-24.1,1) rot=(0.707107,0,0.707107;3.14159rad)
  Placement2 = pos=(31.32,24.1,1) rot=(0.707107,0,0.707107;3.14159rad)
  Reference1 = -> Assembly [Assembly021.Assembly022.Body029.Edge120,Assembly021.Assembly022.Body029.Edge120]
  Reference2 = -> Assembly [Assembly016.Assembly017.Body022.Edge112,Assembly016.Assembly017.Body022.Edge112]
  Suppressed = false
FEATURE [Assembly::JointGroup] Joints
  Group = -> [Joint,GroundedJoint,Joint001,Joint002,Joint003]
FEATURE [Assembly::AssemblyObject] Assembly
  Group = -> [Joints,Assembly001,Assembly006,Assembly011,Assembly016,Assembly021,Joint,GroundedJoint,Joint001,Joint002,Joint003]
  Origin = -> Origin
  Type = Assembly

RESOLVED EXTERNAL PARTS (link-assembly join: the EXTERNAL_REF files above that resolve inside this repo's crawl, each included once):
---- part K93-10436-H7-L120_Tarantinorino_left_withFeet.FCStd = doc fcstd_c7ecf6655185 ----
FCSTD DOCUMENT  (FreeCAD 1.1R20251031 (Git shallow))
Label: K93-10436-H7-L120_Tarantinorino_left_withFeet
License: All rights reserved
LicenseURL: https://en.wikipedia.org/wiki/All_rights_reserved
objects: App::Link×3, App::FeaturePython×3, App::Point×1, Assembly::JointGroup×1, Assembly::AssemblyObject×1
EXTERNAL_REF file=K93-10436-H7-L120_Tarantinorino_left.FCStd obj=Body
EXTERNAL_REF file=3M_SJ5382.FCStd obj=Body

FEATURE [App::Point] Origin001
  Role = Origin
FEATURE [App::Link] Body
  LinkPlacement = pos=(-62,-13.9,-4.09999) rot=(1,0,0;1.5708rad)
  LinkedObject = -> <external K93-10436-H7-L120_Tarantinorino_left.FCStd>#Body
  Placement = pos=(-62,-13.9,-4.09999) rot=(1,0,0;1.5708rad)
FEATURE [App::FeaturePython] GroundedJoint  label="GroundedJoint001"  # Assembly grounded joint (typed FeaturePython)
  ObjectToGround = -> Body
FEATURE [App::Link] _3M_SJ5382  label="3M_SJ5382"
  LinkPlacement = pos=(-9.29583,-1.9,-4.09999) rot=(0.57735,0.57735,0.57735;2.0944rad)
  LinkedObject = -> <external 3M_SJ5382.FCStd>#Body
  Placement = pos=(-9.29583,-1.9,-4.09999) rot=(0.57735,0.57735,0.57735;2.0944rad)
FEATURE [App::FeaturePython] Joint  label="Fixed"  # Assembly joint (typed FeaturePython)
  Angle = 0
  AngleMax = 0
  AngleMin = 0
  Detach1 = false
  Detach2 = false
  Distance = 0
  Distance2 = 0
  EnableAngleMax = false
  EnableAngleMin = false
  EnableLengthMax = false
  EnableLengthMin = false
  JointType = 0 (Fixed)
  LengthMax = 0
  LengthMin = 0
  Placement1 = pos=(52.7042,1.8e-15,-12) rot=(-0.707107,0,-0.707107;3.14159rad)
  Placement2 = pos=(0,0,0) rot=(0,0,-1;3.14159rad)
  Reference1 = -> Assembly [Body.Face83,Body.Face83]
  Reference2 = -> Assembly [_3M_SJ5382.Face3,_3M_SJ5382.Face3]
  Suppressed = false
FEATURE [App::Link] _3M_SJ5383  label="3M_SJ5383"
  LinkPlacement = pos=(-30.6801,-1.9,-32.2) rot=(0.707107,-0.707107,0;3.14159rad)
  LinkedObject = -> <external 3M_SJ5382.FCStd>#Body
  Placement = pos=(-30.6801,-1.9,-32.2) rot=(0.707107,-0.707107,0;3.14159rad)
FEATURE [App::FeaturePython] Joint001  label="Fixed004"  # Assembly joint (typed FeaturePython)
  Angle = 0
  AngleMax = 0
  AngleMin = 0
  Detach1 = false
  Detach2 = false
  Distance = 0
  Distance2 = 0
  EnableAngleMax = false
  EnableAngleMin = false
  EnableLengthMax = false
  EnableLengthMin = false
  JointType = 0 (Fixed)
  LengthMax = 0
  LengthMin = 0
  Placement1 = pos=(0,0,0) rot=(-1,0,0;3.14159rad)
  Placement2 = pos=(31.32,-28.1,-12) rot=(-0.57735,-0.57735,-0.57735;2.0944rad)
  Reference1 = -> Assembly [_3M_SJ5383.Edge4,_3M_SJ5383.Edge4]
  Reference2 = -> Assembly [Body.Face129,Body.Face129]
  Suppressed = false
FEATURE [Assembly::JointGroup] Joints
  Group = -> [GroundedJoint,Joint,Joint001]
FEATURE [Assembly::AssemblyObject] Assembly
  Group = -> [Joints,Body,GroundedJoint,_3M_SJ5382,Joint,_3M_SJ5383,Joint001]
  Origin = -> Origin
  Type = Assembly
---- part K93-10436-H7-L120_Tarantinorino_right_withFeet.FCStd = doc fcstd_a3d1782a5d18 ----
FCSTD DOCUMENT  (FreeCAD 1.1R20251031 (Git shallow))
Label: K93-10436-H7-L120_Tarantinorino_right_withFeet
License: All rights reserved
LicenseURL: https://en.wikipedia.org/wiki/All_rights_reserved
objects: App::Link×3, App::FeaturePython×3, App::Point×1, Assembly::JointGroup×1, Assembly::AssemblyObject×1
EXTERNAL_REF file=K93-10436-H7-L120_Tarantinorino_right.FCStd obj=Part__Mirroring
EXTERNAL_REF file=3M_SJ5382.FCStd obj=Body

FEATURE [App::Point] Origin001
  Role = Origin
FEATURE [App::Link] Body__Mirror__1_  label="Body (Mirror #1)"
  LinkPlacement = pos=(1.43051e-06,-13.9,-10.1) rot=(1,0,0;1.5708rad)
  LinkedObject = -> <external K93-10436-H7-L120_Tarantinorino_right.FCStd>#Part__Mirroring
  Placement = pos=(1.43051e-06,-13.9,-10.1) rot=(1,0,0;1.5708rad)
FEATURE [App::FeaturePython] GroundedJoint  # Assembly grounded joint (typed FeaturePython)
  ObjectToGround = -> Body__Mirror__1_
FEATURE [App::Link] _3M_SJ5382  label="3M_SJ5382"
  LinkPlacement = pos=(-31.32,-1.89999,-37) rot=(0.707107,0.707107,0;3.14159rad)
  LinkedObject = -> <external 3M_SJ5382.FCStd>#Body
  Placement = pos=(-31.32,-1.89999,-37) rot=(0.707107,0.707107,0;3.14159rad)
FEATURE [App::FeaturePython] Joint  label="Fixed"  # Assembly joint (typed FeaturePython)
  Angle = 0
  AngleMax = 0
  AngleMin = 0
  Detach1 = false
  Detach2 = false
  Distance = 0
  Distance2 = 0
  EnableAngleMax = false
  EnableAngleMin = false
  EnableLengthMax = false
  EnableLengthMin = false
  JointType = 0 (Fixed)
  LengthMax = 0
  LengthMin = 0
  Placement1 = pos=(-31.32,-26.9,-12) rot=(-0.57735,0.57735,-0.57735;4.18879rad)
  Placement2 = pos=(0,0,0) rot=(0,0,-1;3.14159rad)
  Reference1 = -> Assembly [Body__Mirror__1_.Face111,Body__Mirror__1_.Face111]
  Reference2 = -> Assembly [_3M_SJ5382.?Face3,_3M_SJ5382.?Edge1]
  Suppressed = false
FEATURE [App::Link] _3M_SJ5383  label="3M_SJ5383"
  LinkPlacement = pos=(-52.7042,-1.9,-10.1) rot=(-0.57735,-0.57735,0.57735;2.0944rad)
  LinkedObject = -> <external 3M_SJ5382.FCStd>#Body
  Placement = pos=(-52.7042,-1.9,-10.1) rot=(-0.57735,-0.57735,0.57735;2.0944rad)
FEATURE [App::FeaturePython] Joint001  label="Fixed001"  # Assembly joint (typed FeaturePython)
  Angle = 0
  AngleMax = 0
  AngleMin = 0
  Detach1 = false
  Detach2 = false
  Distance = 0
  Distance2 = 0
  EnableAngleMax = false
  EnableAngleMin = false
  EnableLengthMax = false
  EnableLengthMin = false
  JointType = 0 (Fixed)
  LengthMax = 0
  LengthMin = 0
  Placement1 = pos=(-52.7042,0,-12) rot=(-0.707107,0,-0.707107;3.14159rad)
  Placement2 = pos=(0,0,0) rot=(0,0,1;3.14159rad)
  Reference1 = -> Assembly [Body__Mirror__1_.Face106,Body__Mirror__1_.Face106]
  Reference2 = -> Assembly [_3M_SJ5383.?Face3,_3M_SJ5383.?Face3]
  Suppressed = false
FEATURE [Assembly::JointGroup] Joints
  Group = -> [GroundedJoint,Joint,Joint001]
FEATURE [Assembly::AssemblyObject] Assembly
  Group = -> [Joints,Body__Mirror__1_,GroundedJoint,_3M_SJ5382,Joint,_3M_SJ5383,Joint001]
  Origin = -> Origin
  Type = Assembly
---- part generated_example_K93-10436_all7_withTarantinorinos.FCStd = doc fcstd_a31de3788964 ----
FCSTD DOCUMENT  (FreeCAD 1.1R20251031 (Git shallow))
Label: generated_example_K93-10436_all7_withTarantinorinos
License: All rights reserved
LicenseURL: https://en.wikipedia.org/wiki/All_rights_reserved
objects: App::Link×19, App::FeaturePython×14, App::Point×5, Assembly::AssemblyLink×4, Assembly::JointGroup×1, Assembly::AssemblyObject×1
EXTERNAL_REF file=K93-10436-H7-L120.FCStd obj=K93_120
EXTERNAL_REF file=Reference_all7.FCStd obj=Reference_all7_1
EXTERNAL_REF file=K93-10436-H7-L120_frontpanel_generated_example.FCStd obj=Body
EXTERNAL_REF file=K93-10436-H7-L120_Tarantinorino_left_withFeet.FCStd obj=Assembly
EXTERNAL_REF file=K93-10436-H7-L120_Tarantinorino_left_withFeet.FCStd obj=_3M_SJ5382
EXTERNAL_REF file=K93-10436-H7-L120_Tarantinorino_left_withFeet.FCStd obj=_3M_SJ5383
EXTERNAL_REF file=K93-10436-H7-L120_Tarantinorino_left_withFeet.FCStd obj=Body
EXTERNAL_REF file=K93-10436-H7-L120_Tarantinorino_right_withFeet.FCStd obj=Assembly
EXTERNAL_REF file=K93-10436-H7-L120_Tarantinorino_right_withFeet.FCStd obj=Body__Mirror__1_
EXTERNAL_REF file=K93-10436-H7-L120_Tarantinorino_right_withFeet.FCStd obj=_3M_SJ5382
EXTERNAL_REF file=K93-10436-H7-L120_Tarantinorino_right_withFeet.FCStd obj=_3M_SJ5383
EXTERNAL_REF file=K93-10436-H7-L120_Bumperino.FCStd obj=Body

FEATURE [App::Link] K93_120  label="K93-120"
  LinkPlacement = pos=(0,126.938,111.562) rot=(1,0,0;1.5708rad)
  LinkedObject = -> <external K93-10436-H7-L120.FCStd>#K93_120
  Placement = pos=(0,126.938,111.562) rot=(1,0,0;1.5708rad)
FEATURE [App::FeaturePython] GroundedJoint  # Assembly grounded joint (typed FeaturePython)
  ObjectToGround = -> K93_120
  Placement = pos=(0,126.938,111.562) rot=(1,0,0;1.5708rad)
FEATURE [App::Link] Reference_all7_1  label="Reference_all7 1"
  LinkPlacement = pos=(2.87919,6.93809,110.59) rot=(0.99808,0,0;0rad)
  LinkedObject = -> <external Reference_all7.FCStd>#Reference_all7_1
  Placement = pos=(2.87919,6.93809,110.59) rot=(0.99808,0,0;0rad)
FEATURE [App::FeaturePython] Joint  label="Distance"  # Assembly joint (typed FeaturePython)
  Angle = 0
  AngleMax = 0
  AngleMin = 0
  Detach1 = false
  Detach2 = false
  Distance = -0.2
  Distance2 = 0
  EnableAngleMax = false
  EnableAngleMin = false
  EnableLengthMax = false
  EnableLengthMin = false
  JointType = 5 (Distance)
  LengthMax = 0
  LengthMin = 0
  Offset1 = pos=(0,0,0) rot=(0,0,1;3.14159rad)
  Placement1 = pos=(-50,10.1,0) rot=(-0.707107,0,0.707107;3.14159rad)
  Placement2 = pos=(-49.8,1.8e-15,0.755) rot=(-0.57735,-0.57735,0.57735;2.0944rad)
  Reference1 = -> Assembly [K93_120.Part__Feature.Face87,K93_120.Part__Feature.Vertex159]
  Reference2 = -> Assembly [Reference_all7_1.Part__Feature426.Face3,Reference_all7_1.Part__Feature426.Vertex3]
  Suppressed = false
FEATURE [App::FeaturePython] Joint001  label="Distance001"  # Assembly joint (typed FeaturePython)
  Angle = 0
  AngleMax = 0
  AngleMin = 0
  Detach1 = false
  Detach2 = false
  Distance = 0.2
  Distance2 = 0
  EnableAngleMax = false
  EnableAngleMin = false
  EnableLengthMax = false
  EnableLengthMin = false
  JointType = 5 (Distance)
  LengthMax = 0
  LengthMin = 0
  Placement1 = pos=(4e-16,-59.8,0.755) rot=(0,-0.707107,0.707107;3.14159rad)
  Placement2 = pos=(1.58751,4.42551,60) rot=(0,0,1;0rad)
  Reference1 = -> Assembly [Reference_all7_1.Part__Feature426.Face1,Reference_all7_1.Part__Feature426.Vertex4]
  Reference2 = -> Assembly [K93_120.Part__Feature.Face58,K93_120.Part__Feature.Vertex116]
  Suppressed = false
FEATURE [App::FeaturePython] Joint002  label="Distance002"  # Assembly joint (typed FeaturePython)
  Angle = 0
  AngleMax = 0
  AngleMin = 0
  Detach1 = false
  Detach2 = false
  Distance = 0.25
  Distance2 = 0
  EnableAngleMax = false
  EnableAngleMin = false
  EnableLengthMax = false
  EnableLengthMin = false
  JointType = 5 (Distance)
  LengthMax = 0
  LengthMin = 0
  Placement1 = pos=(-48.85,11.1,0) rot=(-0.57735,-0.57735,0.57735;4.18879rad)
  Placement2 = pos=(0.0111337,0.109635,1.51) rot=(0,0,1;0rad)
  Reference1 = -> Assembly [K93_120.Part__Feature.Face78,K93_120.Part__Feature.Vertex160]
  Reference2 = -> Assembly [Reference_all7_1.Part__Feature426.Face5,Reference_all7_1.Part__Feature426.Vertex3]
  Suppressed = false
FEATURE [App::Link] Body
  LinkPlacement = pos=(2.87919,-53.8119,119.256) rot=(1,0,0;1.5708rad)
  LinkedObject = -> <external K93-10436-H7-L120_frontpanel_generated_example.FCStd>#Body
  Placement = pos=(2.87919,-53.8119,119.256) rot=(1,0,0;1.5708rad)
FEATURE [App::FeaturePython] Joint003  label="Fixed"  # Assembly joint (typed FeaturePython)
  Angle = 0
  AngleMax = 0
  AngleMin = 0
  Detach1 = false
  Detach2 = false
  Distance = 0
  Distance2 = 0
  EnableAngleMax = false
  EnableAngleMin = false
  EnableLengthMax = false
  EnableLengthMin = false
  JointType = 0 (Fixed)
  LengthMax = 0
  LengthMin = 0
  Offset2 = pos=(0,0,0) rot=(0,0,1;3.14159rad)
  Placement1 = pos=(9.8e-15,0,60) rot=(0.707107,0,0.707107;3.14159rad)
  Placement2 = pos=(1.5001e-12,17.9943,-0.75) rot=(0,1,0;4.71239rad)
  Reference1 = -> Assembly [K93_120.Part__Feature001.Edge190,K93_120.Part__Feature001.Edge190]
  Reference2 = -> Assembly [Body.Edge39,Body.Edge39]
  Suppressed = false
FEATURE [App::Point] Origin001  label="Origin"
  Role = Origin
FEATURE [App::Point] Origin003
  Role = Origin
FEATURE [App::Link] _3M_SJ5382  label="3M_SJ5382"
  LinkPlacement = pos=(-9.29583,-1.9,-4.09999) rot=(0.57735,0.57735,0.57735;2.0944rad)
  LinkedObject = -> <external K93-10436-H7-L120_Tarantinorino_left_withFeet.FCStd>#_3M_SJ5382
  Placement = pos=(-9.29583,-1.9,-4.09999) rot=(0.57735,0.57735,0.57735;2.0944rad)
FEATURE [App::Link] _3M_SJ5383  label="3M_SJ5383"
  LinkPlacement = pos=(-30.6801,-1.9,-32.2) rot=(0.707107,-0.707107,0;3.14159rad)
  LinkedObject = -> <external K93-10436-H7-L120_Tarantinorino_left_withFeet.FCStd>#_3M_SJ5383
  Placement = pos=(-30.6801,-1.9,-32.2) rot=(0.707107,-0.707107,0;3.14159rad)
FEATURE [App::Link] Body001
  LinkPlacement = pos=(-62,-13.9,-4.09999) rot=(1,0,0;1.5708rad)
  LinkedObject = -> <external K93-10436-H7-L120_Tarantinorino_left_withFeet.FCStd>#Body
  Placement = pos=(-62,-13.9,-4.09999) rot=(1,0,0;1.5708rad)
FEATURE [Assembly::AssemblyLink] Assembly001  label="Assembly"
  Group = -> [_3M_SJ5382,_3M_SJ5383,Body001]
  LinkedObject = -> <external K93-10436-H7-L120_Tarantinorino_left_withFeet.FCStd>#Assembly
  Origin = -> Origin002
  Placement = pos=(64.9193,-40.6619,123.46) rot=(0,0,1;0rad)
  Rigid = true
FEATURE [App::FeaturePython] Joint004  label="Revolute003"  # Assembly joint (typed FeaturePython)
  Angle = 0
  AngleMax = 0
  AngleMin = 0
  Detach1 = false
  Detach2 = false
  Distance = 0
  Distance2 = 0
  EnableAngleMax = false
  EnableAngleMin = false
  EnableLengthMax = false
  EnableLengthMin = false
  JointType = 1 (Revolute)
  LengthMax = 0
  LengthMin = 0
  Placement1 = pos=(47.26,11.84,1.8e-15) rot=(0,0,1;0rad)
  Placement2 = pos=(47.3,11.9443,0.75) rot=(-1,0,0;3.14159rad)
  Reference1 = -> Assembly [Assembly001.Body001.?Edge32,Assembly001.Body001.?Edge32]
  Reference2 = -> Assembly [Body.Edge34,Body.Edge34]
  Suppressed = false
FEATURE [App::FeaturePython] Joint005  label="Parallel003"  # Assembly joint (typed FeaturePython)
  Angle = 0
  AngleMax = 0
  AngleMin = 0
  Detach1 = false
  Detach2 = false
  Distance = 0
  Distance2 = 0
  EnableAngleMax = false
  EnableAngleMin = false
  EnableLengthMax = false
  EnableLengthMin = false
  JointType = 6 (Parallel)
  LengthMax = 0
  LengthMin = 0
  Placement1 = pos=(52,11.7142,0) rot=(-0.57735,0.57735,0.57735;4.18879rad)
  Placement2 = pos=(52.1042,2.7e-15,-13) rot=(-0.707107,0,0.707107;3.14159rad)
  Reference1 = -> Assembly [K93_120.Part__Feature.Face11,K93_120.Part__Feature.Face11]
  Reference2 = -> Assembly [Assembly001.Body001.?Face16,Assembly001.Body001.?Face16]
  Suppressed = false
FEATURE [App::Point] Origin005  label="Origin006"
  Role = Origin
FEATURE [App::Link] _3M_SJ5384  label="3M_SJ5384"
  LinkPlacement = pos=(-9.29583,-1.9,-4.09999) rot=(0.57735,0.57735,0.57735;2.0944rad)
  LinkedObject = -> <external K93-10436-H7-L120_Tarantinorino_left_withFeet.FCStd>#_3M_SJ5382
  Placement = pos=(-9.29583,-1.9,-4.09999) rot=(0.57735,0.57735,0.57735;2.0944rad)
FEATURE [App::Link] _3M_SJ5385  label="3M_SJ5385"
  LinkPlacement = pos=(-30.6801,-1.9,-32.2) rot=(0.707107,-0.707107,0;3.14159rad)
  LinkedObject = -> <external K93-10436-H7-L120_Tarantinorino_left_withFeet.FCStd>#_3M_SJ5383
  Placement = pos=(-30.6801,-1.9,-32.2) rot=(0.707107,-0.707107,0;3.14159rad)
FEATURE [App::Link] Body002
  LinkPlacement = pos=(-62,-13.9,-4.09999) rot=(1,0,0;1.5708rad)
  LinkedObject = -> <external K93-10436-H7-L120_Tarantinorino_left_withFeet.FCStd>#Body
  Placement = pos=(-62,-13.9,-4.09999) rot=(1,0,0;1.5708rad)
FEATURE [Assembly::AssemblyLink] Assembly002  label="Assembly"
  Group = -> [_3M_SJ5384,_3M_SJ5385,Body002]
  LinkedObject = -> <external K93-10436-H7-L120_Tarantinorino_left_withFeet.FCStd>#Assembly
  Origin = -> Origin004
  Placement = pos=(-59.1609,54.5381,123.46) rot=(0,0,1;3.14159rad)
  Rigid = true
FEATURE [App::FeaturePython] Joint006  label="Fixed003"  # Assembly joint (typed FeaturePython)
  Angle = 0
  AngleMax = 0
  AngleMin = 0
  Detach1 = false
  Detach2 = false
  Distance = 0
  Distance2 = 0
  EnableAngleMax = false
  EnableAngleMin = false
  EnableLengthMax = false
  EnableLengthMin = false
  JointType = 0 (Fixed)
  LengthMax = 0
  LengthMin = 0
  Placement1 = pos=(47.3,11.9443,0.75) rot=(-1,0,0;3.14159rad)
  Placement2 = pos=(47.26,11.84,1.8e-15) rot=(0,0,1;0rad)
  Reference1 = -> Assembly [K93_120.Part__Feature003.Edge10,K93_120.Part__Feature003.Edge10]
  Reference2 = -> Assembly [Assembly002.Body002.?Edge32,Assembly002.Body002.?Edge32]
  Suppressed = false
FEATURE [App::Point] Origin007  label="Origin009"
  Role = Origin
FEATURE [App::Link] Body__Mirror__1_  label="Body (Mirror #1)"
  LinkPlacement = pos=(1.43051e-06,-13.9,-10.1) rot=(1,0,0;1.5708rad)
  LinkedObject = -> <external K93-10436-H7-L120_Tarantinorino_right_withFeet.FCStd>#Body__Mirror__1_
  Placement = pos=(1.43051e-06,-13.9,-10.1) rot=(1,0,0;1.5708rad)
FEATURE [App::Link] _3M_SJ5386  label="3M_SJ5386"
  LinkPlacement = pos=(-31.32,-1.89999,-37) rot=(0.707107,0.707107,0;3.14159rad)
  LinkedObject = -> <external K93-10436-H7-L120_Tarantinorino_right_withFeet.FCStd>#_3M_SJ5382
  Placement = pos=(-31.32,-1.89999,-37) rot=(0.707107,0.707107,0;3.14159rad)
FEATURE [App::Link] _3M_SJ5387  label="3M_SJ5387"
  LinkPlacement = pos=(-52.7042,-1.9,-10.1) rot=(-0.57735,-0.57735,0.57735;2.0944rad)
  LinkedObject = -> <external K93-10436-H7-L120_Tarantinorino_right_withFeet.FCStd>#_3M_SJ5383
  Placement = pos=(-52.7042,-1.9,-10.1) rot=(-0.57735,-0.57735,0.57735;2.0944rad)
FEATURE [Assembly::AssemblyLink] Assembly003  label="Assembly"
  Group = -> [Body__Mirror__1_,_3M_SJ5386,_3M_SJ5387]
  LinkedObject = -> <external K93-10436-H7-L120_Tarantinorino_right_withFeet.FCStd>#Assembly
  Origin = -> Origin006
  Placement = pos=(2.91922,54.5381,129.46) rot=(0,0,1;3.14159rad)
  Rigid = true
FEATURE [App::Point] Origin009  label="Origin011"
  Role = Origin
FEATURE [App::Link] Body__Mirror__1_001  label="Body (Mirror #1)001"
  LinkPlacement = pos=(1.43051e-06,-13.9,-10.1) rot=(1,0,0;1.5708rad)
  LinkedObject = -> <external K93-10436-H7-L120_Tarantinorino_right_withFeet.FCStd>#Body__Mirror__1_
  Placement = pos=(1.43051e-06,-13.9,-10.1) rot=(1,0,0;1.5708rad)
FEATURE [App::Link] _3M_SJ5388  label="3M_SJ5388"
  LinkPlacement = pos=(-31.32,-1.89999,-37) rot=(0.707107,0.707107,0;3.14159rad)
  LinkedObject = -> <external K93-10436-H7-L120_Tarantinorino_right_withFeet.FCStd>#_3M_SJ5382
  Placement = pos=(-31.32,-1.89999,-37) rot=(0.707107,0.707107,0;3.14159rad)
FEATURE [App::Link] _3M_SJ5389  label="3M_SJ5389"
  LinkPlacement = pos=(-52.7042,-1.9,-10.1) rot=(-0.57735,-0.57735,0.57735;2.0944rad)
  LinkedObject = -> <external K93-10436-H7-L120_Tarantinorino_right_withFeet.FCStd>#_3M_SJ5383
  Placement = pos=(-52.7042,-1.9,-10.1) rot=(-0.57735,-0.57735,0.57735;2.0944rad)
FEATURE [Assembly::AssemblyLink] Assembly004  label="Assembly"
  Group = -> [Body__Mirror__1_001,_3M_SJ5388,_3M_SJ5389]
  LinkedObject = -> <external K93-10436-H7-L120_Tarantinorino_right_withFeet.FCStd>#Assembly
  Origin = -> Origin008
  Placement = pos=(2.83915,-40.6619,129.251) rot=(0,0,1;0rad)
  Rigid = true
FEATURE [App::FeaturePython] Joint007  label="Fixed004"  # Assembly joint (typed FeaturePython)
  Angle = 0
  AngleMax = 0
  AngleMin = 0
  Detach1 = false
  Detach2 = false
  Distance = 0
  Distance2 = 0
  EnableAngleMax = false
  EnableAngleMin = false
  EnableLengthMax = false
  EnableLengthMin = false
  JointType = 0 (Fixed)
  LengthMax = 0
  LengthMin = 0
  Offset2 = pos=(0,0,0) rot=(0,0,1;3.14159rad)
  Placement1 = pos=(-47.3,11.9443,0.75) rot=(-1,0,0;3.14159rad)
  Placement2 = pos=(-47.26,11.84,0) rot=(1,0,0;3.14159rad)
  Reference1 = -> Assembly [K93_120.Part__Feature003.Edge2,K93_120.Part__Feature003.Edge2]
  Reference2 = -> Assembly [Assembly003.Body__Mirror__1_.Edge32,Assembly003.Body__Mirror__1_.Edge32]
  Suppressed = false
FEATURE [App::FeaturePython] Joint008  label="Fixed005"  # Assembly joint (typed FeaturePython)
  Angle = 0
  AngleMax = 0
  AngleMin = 0
  Detach1 = false
  Detach2 = false
  Distance = 0
  Distance2 = 0
  EnableAngleMax = false
  EnableAngleMin = false
  EnableLengthMax = false
  EnableLengthMin = false
  JointType = 0 (Fixed)
  LengthMax = 0
  LengthMin = 0
  Offset2 = pos=(0,0,0) rot=(0,0,1;3.14159rad)
  Placement1 = pos=(-47.26,-11.84,0) rot=(0,1,0;3.14159rad)
  Placement2 = pos=(-47.3,-11.9443,0.75) rot=(0,1,0;3.14159rad)
  Reference1 = -> Assembly [Assembly004.Body__Mirror__1_001.Edge31,Assembly004.Body__Mirror__1_001.Edge31]
  Reference2 = -> Assembly [Body.Edge23,Body.Edge23]
  Suppressed = false
FEATURE [App::Link] Body003
  LinkPlacement = pos=(2.87919,-56.5619,119.047) rot=(1,0,0;1.5708rad)
  LinkedObject = -> <external K93-10436-H7-L120_Bumperino.FCStd>#Body
  Placement = pos=(2.87919,-56.5619,119.047) rot=(1,0,0;1.5708rad)
FEATURE [App::Link] Body004
  LinkPlacement = pos=(2.87919,-56.5619,119.256) rot=(0,0.707107,-0.707107;3.14159rad)
  LinkedObject = -> <external K93-10436-H7-L120_Bumperino.FCStd>#Body
  Placement = pos=(2.87919,-56.5619,119.256) rot=(0,0.707107,-0.707107;3.14159rad)
FEATURE [App::Link] Body005
  LinkPlacement = pos=(2.87919,70.4381,119.256) rot=(-1,0,0;1.5708rad)
  LinkedObject = -> <external K93-10436-H7-L120_Bumperino.FCStd>#Body
  Placement = pos=(2.87919,70.4381,119.256) rot=(-1,0,0;1.5708rad)
FEATURE [App::Link] Body006
  LinkPlacement = pos=(2.87919,70.4381,119.256) rot=(0,0.707107,0.707107;3.14159rad)
  LinkedObject = -> <external K93-10436-H7-L120_Bumperino.FCStd>#Body
  Placement = pos=(2.87919,70.4381,119.256) rot=(0,0.707107,0.707107;3.14159rad)
FEATURE [App::FeaturePython] Joint009  label="Fixed006"  # Assembly joint (typed FeaturePython)
  Angle = 0
  AngleMax = 0
  AngleMin = 0
  Detach1 = false
  Detach2 = false
  Distance = 0
  Distance2 = 0
  EnableAngleMax = false
  EnableAngleMin = false
  EnableLengthMax = false
  EnableLengthMin = false
  JointType = 0 (Fixed)
  LengthMax = 0
  LengthMin = 0
  Offset2 = pos=(0,0,0) rot=(0,0,1;3.14159rad)
  Placement1 = pos=(47.26,11.84,2) rot=(0,0,1;0rad)
  Placement2 = pos=(-47.3,-11.9443,-1.42e-14) rot=(0,-1,0;3.14159rad)
  Reference1 = -> Assembly [Assembly002.Body002.?Edge55,Assembly002.Body002.?Edge55]
  Reference2 = -> Assembly [Body005.Edge23,Body005.Edge23]
  Suppressed = false
FEATURE [App::FeaturePython] Joint010  label="Fixed007"  # Assembly joint (typed FeaturePython)
  Angle = 0
  AngleMax = 0
  AngleMin = 0
  Detach1 = false
  Detach2 = false
  Distance = 0
  Distance2 = 0
  EnableAngleMax = false
  EnableAngleMin = false
  EnableLengthMax = false
  EnableLengthMin = false
  JointType = 0 (Fixed)
  LengthMax = 0
  LengthMin = 0
  Offset2 = pos=(0,0,0) rot=(0,0,1;3.14159rad)
  Placement1 = pos=(-47.26,11.84,2) rot=(0,1,0;3.14159rad)
  Placement2 = pos=(-47.3,11.9443,-1.42e-14) rot=(0,0,1;3.14159rad)
  Reference1 = -> Assembly [Assembly003.Body__Mirror__1_.Edge55,Assembly003.Body__Mirror__1_.Edge55]
  Reference2 = -> Assembly [Body006.Edge22,Body006.Edge22]
  Suppressed = false
FEATURE [App::FeaturePython] Joint011  label="Fixed008"  # Assembly joint (typed FeaturePython)
  Angle = 0
  AngleMax = 0
  AngleMin = 0
  Detach1 = false
  Detach2 = false
  Distance = 0
  Distance2 = 0
  EnableAngleMax = false
  EnableAngleMin = false
  EnableLengthMax = false
  EnableLengthMin = false
  JointType = 0 (Fixed)
  LengthMax = 0
  LengthMin = 0
  Offset2 = pos=(0,0,0) rot=(0,0,1;3.14159rad)
  Placement1 = pos=(-47.26,11.84,2) rot=(0,1,0;3.14159rad)
  Placement2 = pos=(-47.3,11.9443,7.1e-15) rot=(0,0,1;3.14159rad)
  Reference1 = -> Assembly [Assembly004.Body__Mirror__1_001.Edge55,Assembly004.Body__Mirror__1_001.Edge55]
  Reference2 = -> Assembly [Body003.Edge22,Body003.Edge22]
  Suppressed = false
FEATURE [App::FeaturePython] Joint012  label="Fixed009"  # Assembly joint (typed FeaturePython)
  Angle = 0
  AngleMax = 0
  AngleMin = 0
  Detach1 = false
  Detach2 = false
  Distance = 0
  Distance2 = 0
  EnableAngleMax = false
  EnableAngleMin = false
  EnableLengthMax = false
  EnableLengthMin = false
  JointType = 0 (Fixed)
  LengthMax = 0
  LengthMin = 0
  Offset2 = pos=(0,0,0) rot=(0,0,1;3.14159rad)
  Placement1 = pos=(47.26,11.84,2) rot=(0,0,1;0rad)
  Placement2 = pos=(-47.3,-11.9443,0) rot=(0,-1,0;3.14159rad)
  Reference1 = -> Assembly [Assembly001.Body001.?Edge55,Assembly001.Body001.?Edge55]
  Reference2 = -> Assembly [Body004.Edge23,Body004.Edge23]
  Suppressed = false
FEATURE [Assembly::JointGroup] Joints
  Group = -> [GroundedJoint,Joint,Joint001,Joint002,Joint003,Joint004,Joint005,Joint006,Joint007,Joint008,Joint009,Joint010,Joint011,Joint012]
FEATURE [Assembly::AssemblyObject] Assembly
  Group = -> [Joints,K93_120,GroundedJoint,Reference_all7_1,Joint,Joint001,Joint002,Body,Joint003,Assembly001,Joint004,Joint005,Assembly002,Joint006,Assembly003,Assembly004,Joint007,Joint008,Body003,Body004,Body005,Body006,Joint009,Joint010,Joint011,Joint012]
  Origin = -> Origin
  Type = Assembly
